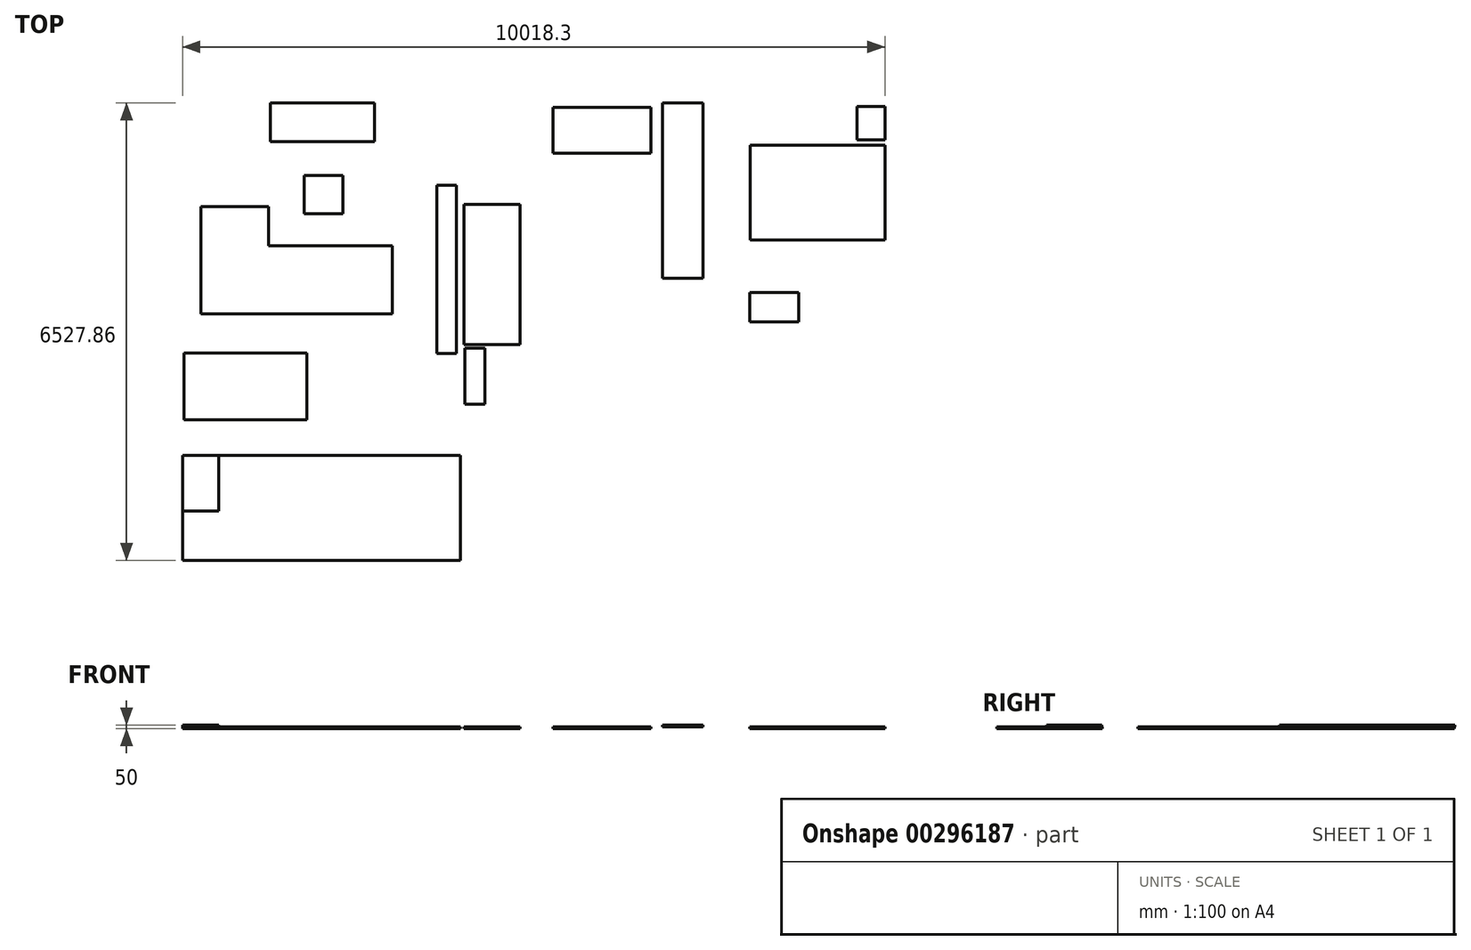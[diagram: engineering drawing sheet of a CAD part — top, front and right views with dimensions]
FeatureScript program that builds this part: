
annotation { "Feature Type Name" : "Feature", "Feature Type Description" : "" }
export const myFeature = defineFeature(function(context is Context, id is Id, definition is map)
    precondition{}
    {
        {
            var Q0;
            Q0=qCreatedBy(makeId("Top.planeOp"),FACE);
            var sketch = newSketch(context, id + "F0", { "sketchPlane" : qUnion([Q0])});
            skLineSegment(sketch, "E0.bottom", {"start": v(-5040.5, 3274) * mm, "end": v(5040.5, 3274) * mm});
            skLineSegment(sketch, "E0.top", {"start": v(-5040.5, -3274) * mm, "end": v(5040.5, -3274) * mm});
            skLineSegment(sketch, "E0.left", {"start": v(-5040.5, 3274) * mm, "end": v(-5040.5, -3274) * mm});
            skLineSegment(sketch, "E0.right", {"start": v(5040.5, 3274) * mm, "end": v(5040.5, -3274) * mm});
            skSolve(sketch);
        }
        {
            var Q0;
            Q0=makeQuery(id+"F0.imprint","IMPRINT",FACE,{"disambiguationData":[TD([[makeQuery(id+"F0.imprint","IMPRINT",EDGE,{"derivedFrom":sQuery(id+"F0.wireOp",EDGE,"E0.bottom")}),-1.0]])]});
            var sketch = newSketch(context, id + "F1", { "sketchPlane" : qUnion([Q0])});
            skLineSegment(sketch, "E1", {"start": v(-1078.5, 3274) * mm, "end": v(-1078.5, -3274) * mm});
            skLineSegment(sketch, "E2", {"start": v(-1078.5, -1109) * mm, "end": v(5040.5, -1109) * mm});
            skLineSegment(sketch, "E3", {"start": v(1741.5, 3274) * mm, "end": v(1741.5, -1109) * mm});
            skLineSegment(sketch, "E4", {"start": v(2983.5, -1109) * mm, "end": v(2983.5, 90) * mm});
            skLineSegment(sketch, "E5", {"start": v(2983.5, 90) * mm, "end": v(5040.5, 90) * mm});
            skLineSegment(sketch, "E6", {"start": v(3168.5, -1109) * mm, "end": v(3168.5, -3274) * mm});
            skLineSegment(sketch, "E7", {"start": v(-1078.5, -2334) * mm, "end": v(1541.5, -2334) * mm});
            skLineSegment(sketch, "E8", {"start": v(1541.5, -2334) * mm, "end": v(1541.5, -3274) * mm});
            skLineSegment(sketch, "E9", {"start": v(741.5, -2334) * mm, "end": v(741.5, -3274) * mm});
            skLineSegment(sketch, "E10", {"start": v(-1078.5, 2774) * mm, "end": v(121.5, 2774) * mm});
            skLineSegment(sketch, "E11", {"start": v(121.5, 2774) * mm, "end": v(121.5, 3274) * mm});
            skSolve(sketch);
        }
        {
            var Q0;
            Q0=makeQuery(id+"F0.imprint","IMPRINT",FACE,{"disambiguationData":[TD([[makeQuery(id+"F0.imprint","IMPRINT",EDGE,{"derivedFrom":sQuery(id+"F0.wireOp",EDGE,"E0.bottom")}),-1.0]])]});
            var sketch = newSketch(context, id + "F2", { "sketchPlane" : qUnion([Q0])});
            skLineSegment(sketch, "E12.bottom", {"start": v(3057.79, 2649.44) * mm, "end": v(4977.79, 2649.44) * mm});
            skLineSegment(sketch, "E12.top", {"start": v(3057.79, 1299.44) * mm, "end": v(4977.79, 1299.44) * mm});
            skLineSegment(sketch, "E12.left", {"start": v(3057.79, 2649.44) * mm, "end": v(3057.79, 1299.44) * mm});
            skLineSegment(sketch, "E12.right", {"start": v(4977.79, 2649.44) * mm, "end": v(4977.79, 1299.44) * mm});
            skSolve(sketch);
        }
        {
            var Q0;
            Q0 = qSketchRegion(id + "F2", true);
            extrude(context, id + "F3", {"entities" : qUnion([Q0]), "depth" : 25 * mm});
        }
        {
            var Q0;
            Q0=makeQuery(id+"F3.opExtrude","CAP_FACE",FACE,{"disambiguationData":[OSD([sQuery(id+"F2.wireOp",EDGE,"E12.bottom"),sQuery(id+"F2.wireOp",EDGE,"E12.top"),sQuery(id+"F2.wireOp",EDGE,"E12.left"),sQuery(id+"F2.wireOp",EDGE,"E12.right")])],"isStart":false});
            var sketch = newSketch(context, id + "F4", { "sketchPlane" : qUnion([Q0])});
            skLineSegment(sketch, "E13.bottom", {"start": v(1806.21, 3253.86) * mm, "end": v(2386.21, 3253.86) * mm});
            skLineSegment(sketch, "E13.top", {"start": v(1806.21, 753.86) * mm, "end": v(2386.21, 753.86) * mm});
            skLineSegment(sketch, "E13.left", {"start": v(1806.21, 3253.86) * mm, "end": v(1806.21, 753.86) * mm});
            skLineSegment(sketch, "E13.right", {"start": v(2386.21, 3253.86) * mm, "end": v(2386.21, 753.86) * mm});
            skSolve(sketch);
        }
        {
            var Q0;
            Q0=makeQuery(id+"F4.imprint","IMPRINT",FACE,{"disambiguationData":[TD([[makeQuery(id+"F4.imprint","IMPRINT",EDGE,{"derivedFrom":sQuery(id+"F4.wireOp",EDGE,"E13.bottom")}),-1.0]])]});
            extrude(context, id + "F5", {"entities" : qUnion([Q0]), "depth" : 25 * mm});
        }
        {
            var Q0;
            {var subQ5=makeQuery(id+"F0.imprint","IMPRINT",EDGE,{"derivedFrom":sQuery(id+"F0.wireOp",EDGE,"E0.left")});Q0=makeQuery(id+"F1.imprint","IMPRINT",FACE,{"disambiguationData":[TD([[makeQuery(id+"F1.imprint","IMPRINT",EDGE,{"derivedFrom":subQ5}),1.0]])]});}
            var sketch = newSketch(context, id + "F6", { "sketchPlane" : qUnion([Q0])});
            skLineSegment(sketch, "E14.bottom", {"start": v(3051.82, 548.22) * mm, "end": v(3751.82, 548.22) * mm});
            skLineSegment(sketch, "E14.top", {"start": v(3051.82, 128.22) * mm, "end": v(3751.82, 128.22) * mm});
            skLineSegment(sketch, "E14.left", {"start": v(3051.82, 548.22) * mm, "end": v(3051.82, 128.22) * mm});
            skLineSegment(sketch, "E14.right", {"start": v(3751.82, 548.22) * mm, "end": v(3751.82, 128.22) * mm});
            skSolve(sketch);
        }
        {
            var Q0;
            Q0 = qSketchRegion(id + "F6", true);
            extrude(context, id + "F7", {"entities" : qUnion([Q0]), "depth" : 25 * mm});
        }
        {
            var Q0;
            {var subQ5=makeQuery(id+"F0.imprint","IMPRINT",EDGE,{"derivedFrom":sQuery(id+"F0.wireOp",EDGE,"E0.left")});Q0=makeQuery(id+"F1.imprint","IMPRINT",FACE,{"disambiguationData":[TD([[makeQuery(id+"F1.imprint","IMPRINT",EDGE,{"derivedFrom":subQ5}),1.0]])]});}
            var sketch = newSketch(context, id + "F8", { "sketchPlane" : qUnion([Q0])});
            skLineSegment(sketch, "E15.bottom", {"start": v(-1024.4, 1805.24) * mm, "end": v(-224.4, 1805.24) * mm});
            skLineSegment(sketch, "E15.top", {"start": v(-1024.4, -194.76) * mm, "end": v(-224.4, -194.76) * mm});
            skLineSegment(sketch, "E15.left", {"start": v(-1024.4, 1805.24) * mm, "end": v(-1024.4, -194.76) * mm});
            skLineSegment(sketch, "E15.right", {"start": v(-224.4, 1805.24) * mm, "end": v(-224.4, -194.76) * mm});
            skSolve(sketch);
        }
        {
            var Q0;
            Q0=makeQuery(id+"F8.imprint","IMPRINT",FACE,{"disambiguationData":[TD([[makeQuery(id+"F8.imprint","IMPRINT",EDGE,{"derivedFrom":sQuery(id+"F8.wireOp",EDGE,"E15.bottom")}),-1.0]])]});
            extrude(context, id + "F9", {"entities" : qUnion([Q0]), "depth" : 25 * mm});
        }
        {
            var Q0;
            {var subQ6=makeQuery(id+"F0.imprint","IMPRINT",EDGE,{"derivedFrom":sQuery(id+"F0.wireOp",EDGE,"E0.left")});Q0=makeQuery(id+"F1.imprint","IMPRINT",FACE,{"disambiguationData":[TD([[makeQuery(id+"F1.imprint","IMPRINT",EDGE,{"derivedFrom":subQ6}),1.0]])]});}
            var sketch = newSketch(context, id + "F10", { "sketchPlane" : qUnion([Q0])});
            skLineSegment(sketch, "E16.bottom", {"start": v(-5040.5, -1774) * mm, "end": v(-1078.5, -1774) * mm});
            skLineSegment(sketch, "E16.top", {"start": v(-5040.5, -3274) * mm, "end": v(-1078.5, -3274) * mm});
            skLineSegment(sketch, "E16.left", {"start": v(-5040.5, -1774) * mm, "end": v(-5040.5, -3274) * mm});
            skLineSegment(sketch, "E16.right", {"start": v(-1078.5, -1774) * mm, "end": v(-1078.5, -3274) * mm});
            skSolve(sketch);
        }
        {
            var Q0;
            Q0 = qSketchRegion(id + "F10", true);
            extrude(context, id + "F11", {"entities" : qUnion([Q0]), "depth" : 25 * mm});
        }
        {
            var Q0;
            Q0=makeQuery(id+"F0.imprint","IMPRINT",FACE,{"disambiguationData":[TD([[makeQuery(id+"F0.imprint","IMPRINT",EDGE,{"derivedFrom":sQuery(id+"F0.wireOp",EDGE,"E0.bottom")}),-1.0]])]});
            var sketch = newSketch(context, id + "F12", { "sketchPlane" : qUnion([Q0])});
            skLineSegment(sketch, "E17", {"start": v(-4781.01, 1774.43) * mm, "end": v(-4781.01, 244.43) * mm});
            skLineSegment(sketch, "E18", {"start": v(-4781.01, 244.43) * mm, "end": v(-2051.01, 244.43) * mm});
            skLineSegment(sketch, "E19", {"start": v(-2051.01, 244.43) * mm, "end": v(-2051.01, 1214.43) * mm});
            skLineSegment(sketch, "E20", {"start": v(-2051.01, 1214.43) * mm, "end": v(-3811.01, 1214.43) * mm});
            skLineSegment(sketch, "E21", {"start": v(-3811.01, 1214.43) * mm, "end": v(-3811.01, 1774.43) * mm});
            skLineSegment(sketch, "E22", {"start": v(-3811.01, 1774.43) * mm, "end": v(-4781.01, 1774.43) * mm});
            skSolve(sketch);
        }
        {
            var Q0;
            Q0 = qSketchRegion(id + "F12", true);
            extrude(context, id + "F13", {"entities" : qUnion([Q0]), "depth" : 25 * mm});
        }
        {
            var Q0;
            Q0=makeQuery(id+"F0.imprint","IMPRINT",FACE,{"disambiguationData":[TD([[makeQuery(id+"F0.imprint","IMPRINT",EDGE,{"derivedFrom":sQuery(id+"F0.wireOp",EDGE,"E0.bottom")}),-1.0]])]});
            var sketch = newSketch(context, id + "F14", { "sketchPlane" : qUnion([Q0])});
            skLineSegment(sketch, "E23.bottom", {"start": v(-5020.79, -316.14) * mm, "end": v(-3270.79, -316.14) * mm});
            skLineSegment(sketch, "E23.top", {"start": v(-5020.79, -1266.14) * mm, "end": v(-3270.79, -1266.14) * mm});
            skLineSegment(sketch, "E23.left", {"start": v(-5020.79, -316.14) * mm, "end": v(-5020.79, -1266.14) * mm});
            skLineSegment(sketch, "E23.right", {"start": v(-3270.79, -316.14) * mm, "end": v(-3270.79, -1266.14) * mm});
            skSolve(sketch);
        }
        {
            var Q0;
            Q0 = qSketchRegion(id + "F14", true);
            extrude(context, id + "F15", {"entities" : qUnion([Q0]), "depth" : 25 * mm});
        }
        {
            var Q0;
            Q0=makeQuery(id+"F0.imprint","IMPRINT",FACE,{"disambiguationData":[TD([[makeQuery(id+"F0.imprint","IMPRINT",EDGE,{"derivedFrom":sQuery(id+"F0.wireOp",EDGE,"E0.bottom")}),-1.0]])]});
            var sketch = newSketch(context, id + "F16", { "sketchPlane" : qUnion([Q0])});
            skLineSegment(sketch, "E24.bottom", {"start": v(4577.79, 3205.64) * mm, "end": v(4977.79, 3205.64) * mm});
            skLineSegment(sketch, "E24.top", {"start": v(4577.79, 2725.64) * mm, "end": v(4977.79, 2725.64) * mm});
            skLineSegment(sketch, "E24.left", {"start": v(4577.79, 3205.64) * mm, "end": v(4577.79, 2725.64) * mm});
            skLineSegment(sketch, "E24.right", {"start": v(4977.79, 3205.64) * mm, "end": v(4977.79, 2725.64) * mm});
            skSolve(sketch);
        }
        {
            var Q0;
            Q0 = qSketchRegion(id + "F16", true);
            extrude(context, id + "F17", {"entities" : qUnion([Q0]), "depth" : 25 * mm});
        }
        {
            var Q0;
            Q0=makeQuery(id+"F0.imprint","IMPRINT",FACE,{"disambiguationData":[TD([[makeQuery(id+"F0.imprint","IMPRINT",EDGE,{"derivedFrom":sQuery(id+"F0.wireOp",EDGE,"E0.bottom")}),-1.0]])]});
            var sketch = newSketch(context, id + "F18", { "sketchPlane" : qUnion([Q0])});
            skLineSegment(sketch, "E25.bottom", {"start": v(240.9, 3188.5) * mm, "end": v(1640.9, 3188.5) * mm});
            skLineSegment(sketch, "E25.top", {"start": v(240.9, 2538.5) * mm, "end": v(1640.9, 2538.5) * mm});
            skLineSegment(sketch, "E25.left", {"start": v(240.9, 3188.5) * mm, "end": v(240.9, 2538.5) * mm});
            skLineSegment(sketch, "E25.right", {"start": v(1640.9, 3188.5) * mm, "end": v(1640.9, 2538.5) * mm});
            skSolve(sketch);
        }
        {
            var Q0;
            Q0 = qSketchRegion(id + "F18", true);
            extrude(context, id + "F19", {"entities" : qUnion([Q0]), "depth" : 25 * mm});
        }
        {
            var Q0;
            Q0=makeQuery(id+"F0.imprint","IMPRINT",FACE,{"disambiguationData":[TD([[makeQuery(id+"F0.imprint","IMPRINT",EDGE,{"derivedFrom":sQuery(id+"F0.wireOp",EDGE,"E0.bottom")}),-1.0]])]});
            var sketch = newSketch(context, id + "F20", { "sketchPlane" : qUnion([Q0])});
            skLineSegment(sketch, "E26.bottom", {"start": v(-1412.19, 2080.96) * mm, "end": v(-1132.19, 2080.96) * mm});
            skLineSegment(sketch, "E26.top", {"start": v(-1412.19, -319.04) * mm, "end": v(-1132.19, -319.04) * mm});
            skLineSegment(sketch, "E26.left", {"start": v(-1412.19, 2080.96) * mm, "end": v(-1412.19, -319.04) * mm});
            skLineSegment(sketch, "E26.right", {"start": v(-1132.19, 2080.96) * mm, "end": v(-1132.19, -319.04) * mm});
            skSolve(sketch);
        }
        {
            var Q0;
            Q0 = qSketchRegion(id + "F20", true);
            extrude(context, id + "F21", {"entities" : qUnion([Q0]), "depth" : 25 * mm});
        }
        {
            var Q0;
            Q0=makeQuery(id+"F0.imprint","IMPRINT",FACE,{"disambiguationData":[TD([[makeQuery(id+"F0.imprint","IMPRINT",EDGE,{"derivedFrom":sQuery(id+"F0.wireOp",EDGE,"E0.bottom")}),-1.0]])]});
            var sketch = newSketch(context, id + "F22", { "sketchPlane" : qUnion([Q0])});
            skLineSegment(sketch, "E27.bottom", {"start": v(-3789.35, 3253.6) * mm, "end": v(-2299.35, 3253.6) * mm});
            skLineSegment(sketch, "E27.top", {"start": v(-3789.35, 2703.6) * mm, "end": v(-2299.35, 2703.6) * mm});
            skLineSegment(sketch, "E27.left", {"start": v(-3789.35, 3253.6) * mm, "end": v(-3789.35, 2703.6) * mm});
            skLineSegment(sketch, "E27.right", {"start": v(-2299.35, 3253.6) * mm, "end": v(-2299.35, 2703.6) * mm});
            skSolve(sketch);
        }
        {
            var Q0;
            Q0 = qSketchRegion(id + "F22", true);
            extrude(context, id + "F23", {"entities" : qUnion([Q0]), "depth" : 25 * mm});
        }
        {
            var Q0;
            Q0=makeQuery(id+"F0.imprint","IMPRINT",FACE,{"disambiguationData":[TD([[makeQuery(id+"F0.imprint","IMPRINT",EDGE,{"derivedFrom":sQuery(id+"F0.wireOp",EDGE,"E0.bottom")}),-1.0]])]});
            var sketch = newSketch(context, id + "F24", { "sketchPlane" : qUnion([Q0])});
            skLineSegment(sketch, "E28.bottom", {"start": v(-3306.4, 2221.09) * mm, "end": v(-2756.4, 2221.09) * mm});
            skLineSegment(sketch, "E28.top", {"start": v(-3306.4, 1671.09) * mm, "end": v(-2756.4, 1671.09) * mm});
            skLineSegment(sketch, "E28.left", {"start": v(-3306.4, 2221.09) * mm, "end": v(-3306.4, 1671.09) * mm});
            skLineSegment(sketch, "E28.right", {"start": v(-2756.4, 2221.09) * mm, "end": v(-2756.4, 1671.09) * mm});
            skSolve(sketch);
        }
        {
            var Q0;
            Q0 = qSketchRegion(id + "F24", true);
            extrude(context, id + "F25", {"entities" : qUnion([Q0]), "depth" : 25 * mm});
        }
        {
            var Q0;
            Q0=makeQuery(id+"F0.imprint","IMPRINT",FACE,{"disambiguationData":[TD([[makeQuery(id+"F0.imprint","IMPRINT",EDGE,{"derivedFrom":sQuery(id+"F0.wireOp",EDGE,"E0.bottom")}),-1.0]])]});
            var sketch = newSketch(context, id + "F26", { "sketchPlane" : qUnion([Q0])});
            skLineSegment(sketch, "E29.bottom", {"start": v(-1010.95, -247.73) * mm, "end": v(-730.95, -247.73) * mm});
            skLineSegment(sketch, "E29.top", {"start": v(-1010.95, -1047.73) * mm, "end": v(-730.95, -1047.73) * mm});
            skLineSegment(sketch, "E29.left", {"start": v(-1010.95, -247.73) * mm, "end": v(-1010.95, -1047.73) * mm});
            skLineSegment(sketch, "E29.right", {"start": v(-730.95, -247.73) * mm, "end": v(-730.95, -1047.73) * mm});
            skSolve(sketch);
        }
        {
            var Q0;
            Q0 = qSketchRegion(id + "F26", true);
            extrude(context, id + "F27", {"entities" : qUnion([Q0]), "depth" : 25 * mm});
        }
        {
            var Q0;
            Q0=makeQuery(id+"F0.imprint","IMPRINT",FACE,{"disambiguationData":[TD([[makeQuery(id+"F0.imprint","IMPRINT",EDGE,{"derivedFrom":sQuery(id+"F0.wireOp",EDGE,"E0.bottom")}),-1.0]])]});
            var sketch = newSketch(context, id + "F28", { "sketchPlane" : qUnion([Q0])});
            skLineSegment(sketch, "E30.bottom", {"start": v(-5037.74, -1776.4) * mm, "end": v(-4527.74, -1776.4) * mm});
            skLineSegment(sketch, "E30.top", {"start": v(-5037.74, -2566.4) * mm, "end": v(-4527.74, -2566.4) * mm});
            skLineSegment(sketch, "E30.left", {"start": v(-5037.74, -1776.4) * mm, "end": v(-5037.74, -2566.4) * mm});
            skLineSegment(sketch, "E30.right", {"start": v(-4527.74, -1776.4) * mm, "end": v(-4527.74, -2566.4) * mm});
            skSolve(sketch);
        }
        {
            var Q0;
            Q0 = qSketchRegion(id + "F28", true);
            extrude(context, id + "F29", {"entities" : qUnion([Q0]), "depth" : 50 * mm});
        }
    });
